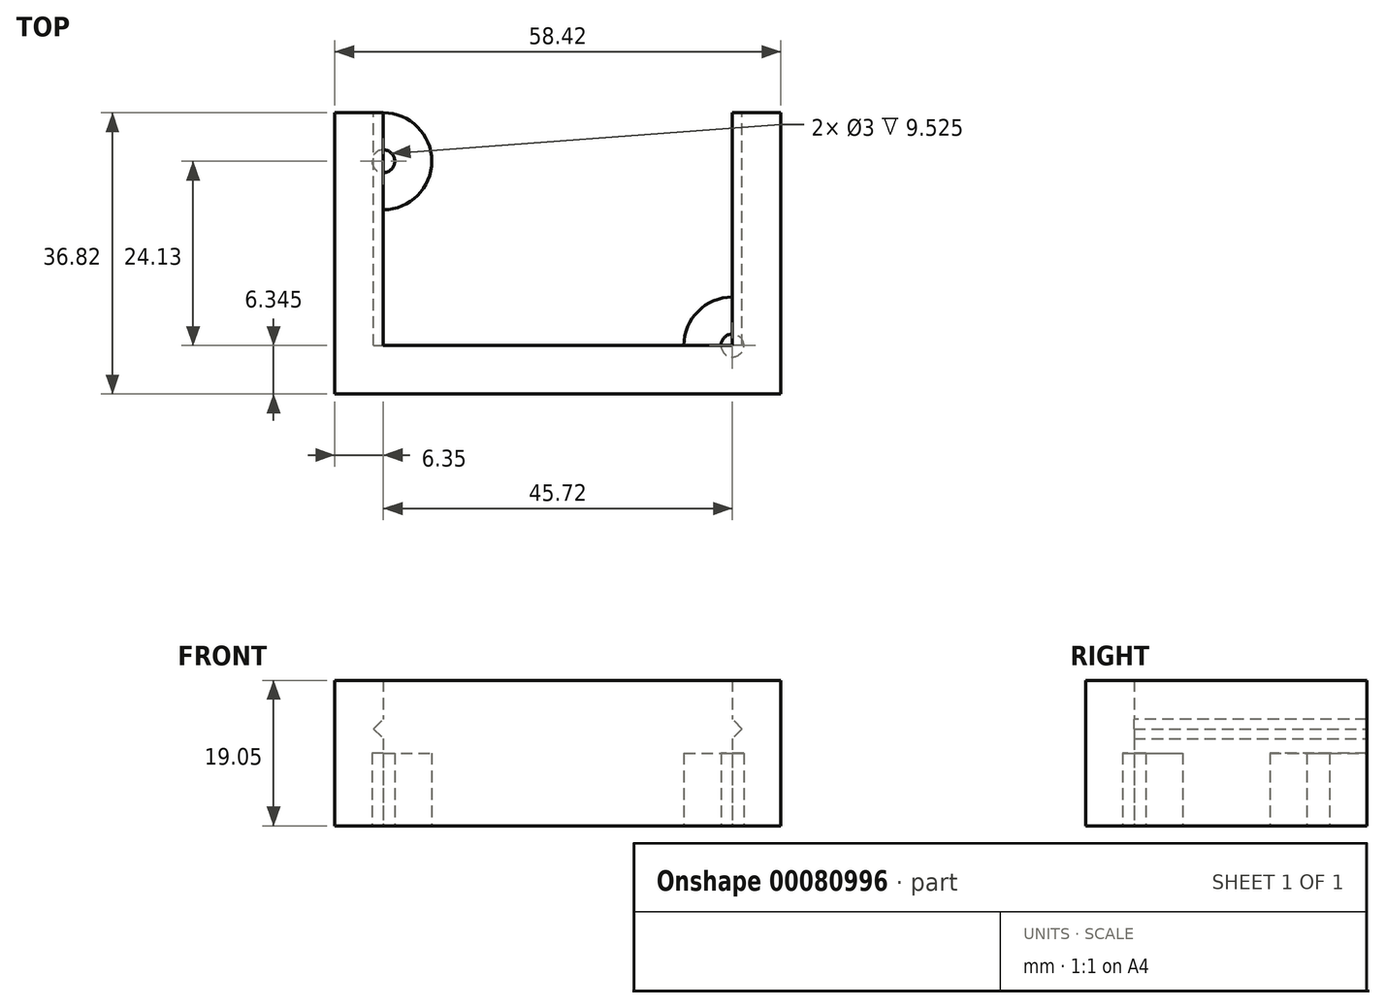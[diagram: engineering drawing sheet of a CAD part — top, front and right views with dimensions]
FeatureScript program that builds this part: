
annotation { "Feature Type Name" : "Feature", "Feature Type Description" : "" }
export const myFeature = defineFeature(function(context is Context, id is Id, definition is map)
    precondition{}
    {
        {
            var Q0;
            Q0=qCreatedBy(makeId("Top.planeOp"),FACE);
            var sketch = newSketch(context, id + "F0", { "sketchPlane" : qUnion([Q0])});
            skLineSegment(sketch, "E0", {"start": v(0, 0) * mm, "end": v(0, 161.12) * mm, "construction": true});
            skLineSegment(sketch, "E1.bottom", {"start": v(-29.2, -18.41) * mm, "end": v(29.2, -18.41) * mm});
            skLineSegment(sketch, "E1.top", {"start": v(-29.2, 18.41) * mm, "end": v(-22.86, 18.41) * mm});
            skLineSegment(sketch, "E1.left", {"start": v(-29.2, -18.41) * mm, "end": v(-29.2, 18.41) * mm});
            skLineSegment(sketch, "E1.right", {"start": v(29.2, -18.41) * mm, "end": v(29.2, 18.41) * mm});
            skPoint(sketch, "E1.middle", {"position": v(0, 0) * mm});
            skLineSegment(sketch, "E2.0", {"start": v(-22.86, -12.07) * mm, "end": v(-22.86, 18.41) * mm});
            skLineSegment(sketch, "E2.1", {"start": v(-22.86, -12.07) * mm, "end": v(22.86, -12.07) * mm});
            skLineSegment(sketch, "E2.2", {"start": v(22.86, -12.07) * mm, "end": v(22.86, 18.41) * mm});
            skLineSegment(sketch, "E3.trimOffspring", {"start": v(22.86, 18.41) * mm, "end": v(29.2, 18.41) * mm});
            skSolve(sketch);
        }
        {
            var Q0;
            Q0=makeQuery(id+"F0.imprint","IMPRINT",FACE,{"disambiguationData":[TD([[makeQuery(id+"F0.imprint","IMPRINT",EDGE,{"derivedFrom":sQuery(id+"F0.wireOp",EDGE,"E1.bottom")}),1.0]])]});
            extrude(context, id + "F1", {"entities" : qUnion([Q0]), "depth" : 6.35 * mm, "hasSecondDirection" : true, "secondDirectionOppositeDirection" : true, "secondDirectionDepth" : 12.7 * mm});
        }
        {
            var Q0;
            Q0=makeQuery(id+"F1.opExtrude","SWEPT_FACE",FACE,{"disambiguationData":[OSD([sQuery(id+"F0.wireOp",EDGE,"E1.top")])]});
            var sketch = newSketch(context, id + "F2", { "sketchPlane" : qUnion([Q0])});
            skLineSegment(sketch, "E4", {"start": v(0, 0) * mm, "end": v(-17.98, 0) * mm, "construction": true});
            skLineSegment(sketch, "E5", {"start": v(-24.13, 0) * mm, "end": v(0, 24.13) * mm});
            skLineSegment(sketch, "E6", {"start": v(0, 0) * mm, "end": v(0, 24.13) * mm, "construction": true});
            skLineSegment(sketch, "E7.MirrorCS", {"start": v(-24.13, 0) * mm, "end": v(0, -24.13) * mm});
            skLineSegment(sketch, "E8.MirrorCS", {"start": v(24.13, 0) * mm, "end": v(0, 24.13) * mm});
            skLineSegment(sketch, "E9.MirrorCS", {"start": v(24.13, 0) * mm, "end": v(0, -24.13) * mm});
            skSolve(sketch);
        }
        {
            var Q0;
            {var subQ6=sQuery(id+"F2.wireOp",EDGE,"E5");Q0=makeQuery(id+"F2.imprint","IMPRINT",FACE,{"disambiguationData":[TD([[makeQuery(id+"F2.imprint","IMPRINT",EDGE,{"derivedFrom":subQ6}),-1.0]])]});}
            var Q1;
            {var subQ0=sQuery(id+"F2.wireOp",EDGE,"E9.MirrorCS");var subQ1=sQuery(id+"F2.wireOp",EDGE,"E8.MirrorCS");var subQ2=makeQuery(id+"F2.imprint","INTERSECT",VERTEX,{"derivedFrom":[subQ1,subQ0]});Q1=makeQuery(id+"F2.imprint","IMPRINT",FACE,{"disambiguationData":[TD([[makeQuery(id+"F2.imprint","IMPRINT",EDGE,{"disambiguationData":[TD([[subQ2,-1.0]])],"derivedFrom":subQ1}),1.0]])]});}
            extrude(context, id + "F3", {"entities" : qUnion([Q0, Q1]), "operationType" : NewBodyOperationType.REMOVE, "oppositeDirection" : true, "depth" : 30.48 * mm});
        }
        {
            var Q0;
            Q0=makeQuery(id+"F1.opExtrude","CAP_FACE",FACE,{"disambiguationData":[OSD([sQuery(id+"F0.wireOp",EDGE,"E1.bottom"),sQuery(id+"F0.wireOp",EDGE,"E1.top"),sQuery(id+"F0.wireOp",EDGE,"E1.left"),sQuery(id+"F0.wireOp",EDGE,"E1.right"),sQuery(id+"F0.wireOp",EDGE,"E2.0"),sQuery(id+"F0.wireOp",EDGE,"E2.1"),sQuery(id+"F0.wireOp",EDGE,"E2.2"),sQuery(id+"F0.wireOp",EDGE,"E3.trimOffspring")])],"isStart":true});
            var sketch = newSketch(context, id + "F4", { "sketchPlane" : qUnion([Q0])});
            skCircle(sketch, "E10", {"center": v(-22.86, -12.06) * mm, "radius": 6.35 * mm});
            skCircle(sketch, "E11", {"center": v(22.86, 12.07) * mm, "radius": 6.35 * mm});
            skSolve(sketch);
        }
        {
            var Q0;
            {var subQ0=sQuery(id+"F4.wireOp",EDGE,"E10");var subQ1=makeQuery(id+"F1.opExtrude","CAP_EDGE",EDGE,{"disambiguationData":[OSD([sQuery(id+"F0.wireOp",EDGE,"E2.0")])],"isStart":true});var subQ3=makeQuery(id+"F4.imprint","INTERSECT",VERTEX,{"derivedFrom":[subQ1,subQ0]});Q0=makeQuery(id+"F4.imprint","IMPRINT",FACE,{"disambiguationData":[TD([[makeQuery(id+"F4.imprint","IMPRINT",EDGE,{"disambiguationData":[TD([[subQ3,1.0]])],"derivedFrom":subQ0}),1.0]])]});}
            var Q1;
            {var subQ0=sQuery(id+"F4.wireOp",EDGE,"E11");var subQ1=makeQuery(id+"F1.opExtrude","CAP_EDGE",EDGE,{"disambiguationData":[OSD([sQuery(id+"F0.wireOp",EDGE,"E2.1")])],"isStart":true});var subQ2=makeQuery(id+"F4.imprint","INTERSECT",VERTEX,{"derivedFrom":[subQ1,subQ0]});Q1=makeQuery(id+"F4.imprint","IMPRINT",FACE,{"disambiguationData":[TD([[makeQuery(id+"F4.imprint","IMPRINT",EDGE,{"disambiguationData":[TD([[subQ2,-1.0]])],"derivedFrom":subQ0}),1.0]])]});}
            extrude(context, id + "F5", {"entities" : qUnion([Q0, Q1]), "operationType" : NewBodyOperationType.ADD, "oppositeDirection" : true, "depth" : 9.52 * mm});
        }
        {
            var Q0;
            {var subQ0=sQuery(id+"F0.wireOp",EDGE,"E2.2");var subQ1=sQuery(id+"F0.wireOp",EDGE,"E2.1");var subQ2=sQuery(id+"F0.wireOp",EDGE,"E2.0");Q0=makeQuery(id+"F5.boolean.opBoolean","MERGE",FACE,{"derivedFrom":[makeQuery(id+"F1.opExtrude","CAP_FACE",FACE,{"disambiguationData":[OSD([sQuery(id+"F0.wireOp",EDGE,"E1.bottom"),sQuery(id+"F0.wireOp",EDGE,"E1.top"),sQuery(id+"F0.wireOp",EDGE,"E1.left"),sQuery(id+"F0.wireOp",EDGE,"E1.right"),subQ2,subQ1,subQ0,sQuery(id+"F0.wireOp",EDGE,"E3.trimOffspring")])],"isStart":true}),makeQuery(id+"F5.opExtrude","CAP_FACE",FACE,{"disambiguationData":[OSD([subQ2,sQuery(id+"F4.wireOp",EDGE,"E10")])],"isStart":true}),makeQuery(id+"F5.opExtrude","CAP_FACE",FACE,{"disambiguationData":[OSD([subQ1,subQ0,sQuery(id+"F4.wireOp",EDGE,"E11")])],"isStart":true})]});}
            var sketch = newSketch(context, id + "F6", { "sketchPlane" : qUnion([Q0])});
            skCircle(sketch, "E12", {"center": v(22.86, 12.07) * mm, "radius": 1.5 * mm});
            skCircle(sketch, "E13", {"center": v(-22.86, -12.06) * mm, "radius": 1.5 * mm});
            skSolve(sketch);
        }
        {
            var Q0;
            Q0=makeQuery(id+"F6.imprint","IMPRINT",FACE,{"disambiguationData":[TD([[makeQuery(id+"F6.imprint","IMPRINT",EDGE,{"derivedFrom":sQuery(id+"F6.wireOp",EDGE,"E12")}),1.0]])]});
            var Q1;
            Q1=makeQuery(id+"F6.imprint","IMPRINT",FACE,{"disambiguationData":[TD([[makeQuery(id+"F6.imprint","IMPRINT",EDGE,{"derivedFrom":sQuery(id+"F6.wireOp",EDGE,"E13")}),1.0]])]});
            extrude(context, id + "F7", {"entities" : qUnion([Q0, Q1]), "operationType" : NewBodyOperationType.REMOVE, "oppositeDirection" : true, "depth" : 9.52 * mm});
        }
    });
